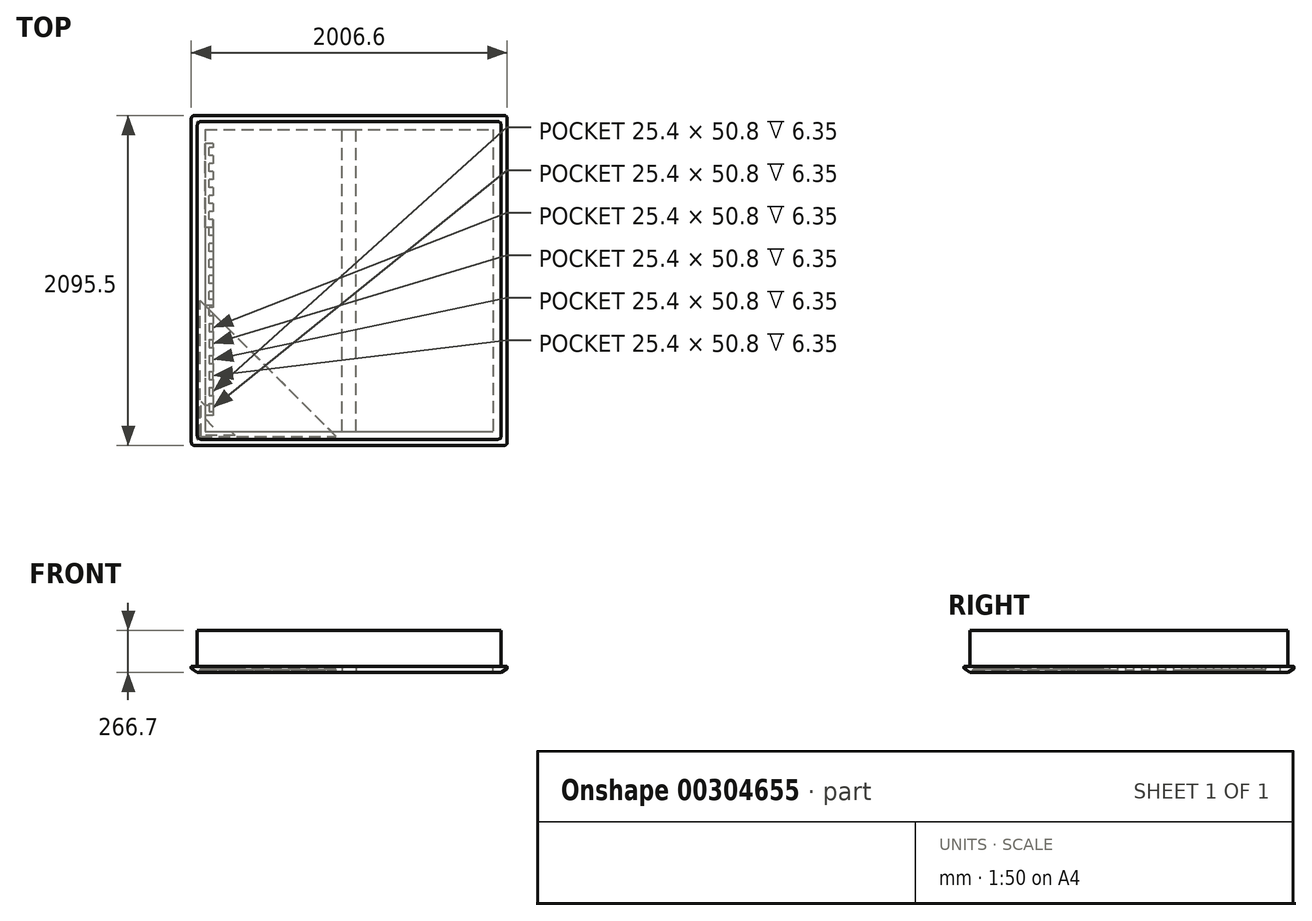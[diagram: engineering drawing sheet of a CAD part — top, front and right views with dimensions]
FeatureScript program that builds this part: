
annotation { "Feature Type Name" : "Feature", "Feature Type Description" : "" }
export const myFeature = defineFeature(function(context is Context, id is Id, definition is map)
    precondition{}
    {
        {
            var Q0;
            Q0=qCreatedBy(makeId("Top.planeOp"),FACE);
            var sketch = newSketch(context, id + "F0", { "sketchPlane" : qUnion([Q0])});
            skLineSegment(sketch, "E0.bottom", {"start": v(-965.2, 1009.65) * mm, "end": v(965.2, 1009.65) * mm});
            skLineSegment(sketch, "E0.top", {"start": v(-965.2, -1009.65) * mm, "end": v(965.2, -1009.65) * mm});
            skLineSegment(sketch, "E0.left", {"start": v(-965.2, 1009.65) * mm, "end": v(-965.2, -1009.65) * mm});
            skLineSegment(sketch, "E0.right", {"start": v(965.2, 1009.65) * mm, "end": v(965.2, -1009.65) * mm});
            skLineSegment(sketch, "E1", {"start": v(-965.2, 1009.65) * mm, "end": v(965.2, -1009.65) * mm, "construction": true});
            skSolve(sketch);
        }
        {
            var Q0;
            Q0=makeQuery(id+"F0.imprint","IMPRINT",FACE,{"disambiguationData":[TD([[makeQuery(id+"F0.imprint","IMPRINT",EDGE,{"derivedFrom":sQuery(id+"F0.wireOp",EDGE,"E0.bottom")}),-1.0]])]});
            extrude(context, id + "F1", {"entities" : qUnion([Q0]), "depth" : 228.6 * mm});
        }
        {
            var Q0;
            Q0=makeQuery(id+"F1.opExtrude","SWEPT_EDGE",EDGE,{"disambiguationData":[OSD([sQuery(id+"F0.wireOp",EDGE,"E0.bottom"),sQuery(id+"F0.wireOp",EDGE,"E0.right")])]});
            var Q1;
            Q1=makeQuery(id+"F1.opExtrude","SWEPT_EDGE",EDGE,{"disambiguationData":[OSD([sQuery(id+"F0.wireOp",EDGE,"E0.top"),sQuery(id+"F0.wireOp",EDGE,"E0.left")])]});
            var Q2;
            Q2=makeQuery(id+"F1.opExtrude","SWEPT_EDGE",EDGE,{"disambiguationData":[OSD([sQuery(id+"F0.wireOp",EDGE,"E0.top"),sQuery(id+"F0.wireOp",EDGE,"E0.right")])]});
            var Q3;
            Q3=makeQuery(id+"F1.opExtrude","SWEPT_EDGE",EDGE,{"disambiguationData":[OSD([sQuery(id+"F0.wireOp",EDGE,"E0.bottom"),sQuery(id+"F0.wireOp",EDGE,"E0.left")])]});
            fillet(context, id + "F2", {"entities" : qUnion([Q0, Q1, Q2, Q3]), "radius" : 25.4 * mm, "tangentPropagation" : true, "allowEdgeOverflow" : false});
        }
        {
            var Q0;
            Q0=qCreatedBy(makeId("Top.planeOp"),FACE);
            var sketch = newSketch(context, id + "F3", { "sketchPlane" : qUnion([Q0])});
            skLineSegment(sketch, "E2.bottom", {"start": v(-1003.3, 1047.75) * mm, "end": v(1003.3, 1047.75) * mm});
            skLineSegment(sketch, "E2.top", {"start": v(-1003.3, -1047.75) * mm, "end": v(1003.3, -1047.75) * mm});
            skLineSegment(sketch, "E2.left", {"start": v(-1003.3, 1047.75) * mm, "end": v(-1003.3, -1047.75) * mm});
            skLineSegment(sketch, "E2.right", {"start": v(1003.3, 1047.75) * mm, "end": v(1003.3, -1047.75) * mm});
            skLineSegment(sketch, "E3.0", {"start": v(-914.4, 958.85) * mm, "end": v(914.4, 958.85) * mm});
            skLineSegment(sketch, "E3.1", {"start": v(-914.4, 958.85) * mm, "end": v(-914.4, -958.85) * mm});
            skLineSegment(sketch, "E3.2", {"start": v(-914.4, -958.85) * mm, "end": v(914.4, -958.85) * mm});
            skLineSegment(sketch, "E3.3", {"start": v(914.4, 958.85) * mm, "end": v(914.4, -958.85) * mm});
            skSolve(sketch);
        }
        {
            var Q0;
            Q0 = qSketchRegion(id + "F3", true);
            extrude(context, id + "F4", {"entities" : qUnion([Q0]), "oppositeDirection" : true, "depth" : 38.1 * mm});
        }
        {
            var Q0;
            Q0=makeQuery(id+"F4.opExtrude","CAP_EDGE",EDGE,{"disambiguationData":[OSD([sQuery(id+"F3.wireOp",EDGE,"E2.left")])],"isStart":false});
            var Q1;
            Q1=makeQuery(id+"F4.opExtrude","CAP_EDGE",EDGE,{"disambiguationData":[OSD([sQuery(id+"F3.wireOp",EDGE,"E2.bottom")])],"isStart":false});
            var Q2;
            Q2=makeQuery(id+"F4.opExtrude","CAP_EDGE",EDGE,{"disambiguationData":[OSD([sQuery(id+"F3.wireOp",EDGE,"E2.top")])],"isStart":false});
            var Q3;
            Q3=makeQuery(id+"F4.opExtrude","CAP_EDGE",EDGE,{"disambiguationData":[OSD([sQuery(id+"F3.wireOp",EDGE,"E2.right")])],"isStart":false});
            chamfer(context, id + "F5", {"entities" : qUnion([Q0, Q1, Q2, Q3]), "chamferType" : ChamferType.TWO_OFFSETS, "width1" : 25.4 * mm, "oppositeDirection" : false, "width2" : 38.1 * mm, "tangentPropagation" : true});
        }
        {
            var Q0;
            Q0=makeQuery(id+"F4.opExtrude","SWEPT_EDGE",EDGE,{"disambiguationData":[OSD([sQuery(id+"F3.wireOp",EDGE,"E2.top"),sQuery(id+"F3.wireOp",EDGE,"E2.right")])]});
            var Q1;
            Q1=makeQuery(id+"F4.opExtrude","SWEPT_EDGE",EDGE,{"disambiguationData":[OSD([sQuery(id+"F3.wireOp",EDGE,"E2.bottom"),sQuery(id+"F3.wireOp",EDGE,"E2.right")])]});
            var Q2;
            Q2=makeQuery(id+"F4.opExtrude","SWEPT_EDGE",EDGE,{"disambiguationData":[OSD([sQuery(id+"F3.wireOp",EDGE,"E2.bottom"),sQuery(id+"F3.wireOp",EDGE,"E2.left")])]});
            var Q3;
            Q3=makeQuery(id+"F4.opExtrude","SWEPT_EDGE",EDGE,{"disambiguationData":[OSD([sQuery(id+"F3.wireOp",EDGE,"E2.top"),sQuery(id+"F3.wireOp",EDGE,"E2.left")])]});
            fillet(context, id + "F6", {"entities" : qUnion([Q0, Q1, Q2, Q3]), "radius" : 19.05 * mm, "allowEdgeOverflow" : false});
        }
        {
            var Q0;
            {var subQ0=sQuery(id+"F3.wireOp",EDGE,"E2.bottom");Q0=makeQuery(id+"F5.opChamfer","BLEND_EDGE",EDGE,{"blendedFrom":[makeQuery(id+"F4.opExtrude","CAP_EDGE",EDGE,{"disambiguationData":[OSD([subQ0])],"isStart":false}),makeQuery(id+"F4.opExtrude","SWEPT_FACE",FACE,{"disambiguationData":[OSD([subQ0])]})],"blendedInto":[makeQuery(id+"F4.opExtrude","SWEPT_FACE",FACE,{"disambiguationData":[OSD([subQ0])]})]});}
            var Q1;
            Q1=makeQuery(id+"F4.opExtrude","CAP_EDGE",EDGE,{"disambiguationData":[OSD([sQuery(id+"F3.wireOp",EDGE,"E2.bottom")])],"isStart":true});
            var Q2;
            Q2=makeQuery(id+"F4.opExtrude","CAP_EDGE",EDGE,{"disambiguationData":[OSD([sQuery(id+"F3.wireOp",EDGE,"E2.left")])],"isStart":true});
            var Q3;
            {var subQ0=sQuery(id+"F3.wireOp",EDGE,"E2.left");Q3=makeQuery(id+"F5.opChamfer","BLEND_EDGE",EDGE,{"blendedFrom":[makeQuery(id+"F4.opExtrude","CAP_EDGE",EDGE,{"disambiguationData":[OSD([subQ0])],"isStart":false}),makeQuery(id+"F4.opExtrude","SWEPT_FACE",FACE,{"disambiguationData":[OSD([subQ0])]})],"blendedInto":[makeQuery(id+"F4.opExtrude","SWEPT_FACE",FACE,{"disambiguationData":[OSD([subQ0])]})]});}
            var Q4;
            Q4=makeQuery(id+"F4.opExtrude","CAP_EDGE",EDGE,{"disambiguationData":[OSD([sQuery(id+"F3.wireOp",EDGE,"E2.top")])],"isStart":true});
            var Q5;
            {var subQ0=sQuery(id+"F3.wireOp",EDGE,"E2.top");Q5=makeQuery(id+"F5.opChamfer","BLEND_EDGE",EDGE,{"blendedFrom":[makeQuery(id+"F4.opExtrude","CAP_EDGE",EDGE,{"disambiguationData":[OSD([subQ0])],"isStart":false}),makeQuery(id+"F4.opExtrude","SWEPT_FACE",FACE,{"disambiguationData":[OSD([subQ0])]})],"blendedInto":[makeQuery(id+"F4.opExtrude","SWEPT_FACE",FACE,{"disambiguationData":[OSD([subQ0])]})]});}
            var Q6;
            {var subQ0=sQuery(id+"F3.wireOp",EDGE,"E2.right");Q6=makeQuery(id+"F5.opChamfer","BLEND_EDGE",EDGE,{"blendedFrom":[makeQuery(id+"F4.opExtrude","CAP_EDGE",EDGE,{"disambiguationData":[OSD([subQ0])],"isStart":false}),makeQuery(id+"F4.opExtrude","SWEPT_FACE",FACE,{"disambiguationData":[OSD([subQ0])]})],"blendedInto":[makeQuery(id+"F4.opExtrude","SWEPT_FACE",FACE,{"disambiguationData":[OSD([subQ0])]})]});}
            var Q7;
            Q7=makeQuery(id+"F4.opExtrude","CAP_EDGE",EDGE,{"disambiguationData":[OSD([sQuery(id+"F3.wireOp",EDGE,"E2.right")])],"isStart":true});
            var Q8;
            Q8=makeQuery(id+"F5.opChamfer","BLEND_EDGE",EDGE,{"blendedFrom":[makeQuery(id+"F4.opExtrude","CAP_EDGE",EDGE,{"disambiguationData":[OSD([sQuery(id+"F3.wireOp",EDGE,"E2.top")])],"isStart":false}),makeQuery(id+"F4.opExtrude","CAP_EDGE",EDGE,{"disambiguationData":[OSD([sQuery(id+"F3.wireOp",EDGE,"E2.right")])],"isStart":false})],"blendedInto":[]});
            var Q9;
            Q9=makeQuery(id+"F4.opExtrude","SWEPT_EDGE",EDGE,{"disambiguationData":[OSD([sQuery(id+"F3.wireOp",EDGE,"E2.top"),sQuery(id+"F3.wireOp",EDGE,"E2.right")])]});
            var Q10;
            Q10=makeQuery(id+"F4.opExtrude","SWEPT_EDGE",EDGE,{"disambiguationData":[OSD([sQuery(id+"F3.wireOp",EDGE,"E2.bottom"),sQuery(id+"F3.wireOp",EDGE,"E2.right")])]});
            var Q11;
            Q11=makeQuery(id+"F5.opChamfer","BLEND_EDGE",EDGE,{"blendedFrom":[makeQuery(id+"F4.opExtrude","CAP_EDGE",EDGE,{"disambiguationData":[OSD([sQuery(id+"F3.wireOp",EDGE,"E2.bottom")])],"isStart":false}),makeQuery(id+"F4.opExtrude","CAP_EDGE",EDGE,{"disambiguationData":[OSD([sQuery(id+"F3.wireOp",EDGE,"E2.right")])],"isStart":false})],"blendedInto":[]});
            var Q12;
            Q12=makeQuery(id+"F4.opExtrude","SWEPT_EDGE",EDGE,{"disambiguationData":[OSD([sQuery(id+"F3.wireOp",EDGE,"E2.bottom"),sQuery(id+"F3.wireOp",EDGE,"E2.left")])]});
            var Q13;
            Q13=makeQuery(id+"F5.opChamfer","BLEND_EDGE",EDGE,{"blendedFrom":[makeQuery(id+"F4.opExtrude","CAP_EDGE",EDGE,{"disambiguationData":[OSD([sQuery(id+"F3.wireOp",EDGE,"E2.bottom")])],"isStart":false}),makeQuery(id+"F4.opExtrude","CAP_EDGE",EDGE,{"disambiguationData":[OSD([sQuery(id+"F3.wireOp",EDGE,"E2.left")])],"isStart":false})],"blendedInto":[]});
            var Q14;
            Q14=makeQuery(id+"F4.opExtrude","SWEPT_EDGE",EDGE,{"disambiguationData":[OSD([sQuery(id+"F3.wireOp",EDGE,"E2.top"),sQuery(id+"F3.wireOp",EDGE,"E2.left")])]});
            var Q15;
            Q15=makeQuery(id+"F5.opChamfer","BLEND_EDGE",EDGE,{"blendedFrom":[makeQuery(id+"F4.opExtrude","CAP_EDGE",EDGE,{"disambiguationData":[OSD([sQuery(id+"F3.wireOp",EDGE,"E2.top")])],"isStart":false}),makeQuery(id+"F4.opExtrude","CAP_EDGE",EDGE,{"disambiguationData":[OSD([sQuery(id+"F3.wireOp",EDGE,"E2.left")])],"isStart":false})],"blendedInto":[]});
            fillet(context, id + "F7", {"entities" : qUnion([Q0, Q1, Q2, Q3, Q4, Q5, Q6, Q7, Q8, Q9, Q10, Q11, Q12, Q13, Q14, Q15]), "radius" : 2.22 * mm, "tangentPropagation" : true, "allowEdgeOverflow" : false});
        }
        {
            var Q0;
            Q0=makeQuery(id+"F4.opExtrude","CAP_FACE",FACE,{"disambiguationData":[OSD([sQuery(id+"F3.wireOp",EDGE,"E2.bottom"),sQuery(id+"F3.wireOp",EDGE,"E2.top"),sQuery(id+"F3.wireOp",EDGE,"E2.left"),sQuery(id+"F3.wireOp",EDGE,"E2.right"),sQuery(id+"F3.wireOp",EDGE,"E3.0"),sQuery(id+"F3.wireOp",EDGE,"E3.1"),sQuery(id+"F3.wireOp",EDGE,"E3.2"),sQuery(id+"F3.wireOp",EDGE,"E3.3")])],"isStart":false});
            var sketch = newSketch(context, id + "F8", { "sketchPlane" : qUnion([Q0])});
            skLineSegment(sketch, "E4.bottom", {"start": v(-946.15, 990.6) * mm, "end": v(-84.05, 990.6) * mm});
            skLineSegment(sketch, "E4.left", {"start": v(-946.15, 990.6) * mm, "end": v(-946.15, 128.5) * mm});
            skLineSegment(sketch, "E5", {"start": v(-84.05, 990.6) * mm, "end": v(-946.15, 128.5) * mm});
            skSolve(sketch);
        }
        {
            var Q0;
            Q0 = qSketchRegion(id + "F8", true);
            extrude(context, id + "F9", {"entities" : qUnion([Q0]), "operationType" : NewBodyOperationType.REMOVE, "oppositeDirection" : true, "depth" : 19.05 * mm});
        }
        {
            var Q0;
            Q0=makeQuery(id+"F9.boolean.opBoolean","COPY",FACE,{"derivedFrom":makeQuery(id+"F9.opExtrude","CAP_FACE",FACE,{"disambiguationData":[OSD([sQuery(id+"F8.wireOp",EDGE,"E4.bottom"),sQuery(id+"F8.wireOp",EDGE,"E4.left"),sQuery(id+"F8.wireOp",EDGE,"E5")])],"isStart":false})});
            var sketch = newSketch(context, id + "F10", { "sketchPlane" : qUnion([Q0])});
            skLineSegment(sketch, "E6.0", {"start": v(-946.15, 990.6) * mm, "end": v(-84.05, 990.6) * mm});
            skLineSegment(sketch, "E6.1", {"start": v(-946.15, 990.6) * mm, "end": v(-946.15, 128.5) * mm});
            skLineSegment(sketch, "E7", {"start": v(-946.15, 128.5) * mm, "end": v(-84.05, 990.6) * mm});
            skSolve(sketch);
        }
        {
            var Q0;
            Q0 = qSketchRegion(id + "F10", true);
            var Q1;
            Q1=makeQuery(id+"F4.opExtrude","CAP_FACE",FACE,{"disambiguationData":[OSD([sQuery(id+"F3.wireOp",EDGE,"E2.bottom"),sQuery(id+"F3.wireOp",EDGE,"E2.top"),sQuery(id+"F3.wireOp",EDGE,"E2.left"),sQuery(id+"F3.wireOp",EDGE,"E2.right"),sQuery(id+"F3.wireOp",EDGE,"E3.0"),sQuery(id+"F3.wireOp",EDGE,"E3.1"),sQuery(id+"F3.wireOp",EDGE,"E3.2"),sQuery(id+"F3.wireOp",EDGE,"E3.3")])],"isStart":false});
            extrude(context, id + "F11", {"entities" : qUnion([Q0]), "endBound" : BoundingType.UP_TO_SURFACE, "endBoundEntityFace" : qUnion([Q1]), "depth" : 12.7 * mm});
        }
        {
            var Q0;
            Q0=makeQuery(id+"F4.opExtrude","CAP_FACE",FACE,{"disambiguationData":[OSD([sQuery(id+"F3.wireOp",EDGE,"E2.bottom"),sQuery(id+"F3.wireOp",EDGE,"E2.top"),sQuery(id+"F3.wireOp",EDGE,"E2.left"),sQuery(id+"F3.wireOp",EDGE,"E2.right"),sQuery(id+"F3.wireOp",EDGE,"E3.0"),sQuery(id+"F3.wireOp",EDGE,"E3.1"),sQuery(id+"F3.wireOp",EDGE,"E3.2"),sQuery(id+"F3.wireOp",EDGE,"E3.3")])],"isStart":true});
            var sketch = newSketch(context, id + "F12", { "sketchPlane" : qUnion([Q0])});
            skLineSegment(sketch, "E8", {"start": v(-724.27, -984.25) * mm, "end": v(-939.8, -984.25) * mm});
            skLineSegment(sketch, "E9", {"start": v(-939.8, -984.25) * mm, "end": v(-939.8, -768.72) * mm});
            skLineSegment(sketch, "E10", {"start": v(-939.8, -768.72) * mm, "end": v(-724.27, -984.25) * mm});
            skSolve(sketch);
        }
        {
            var Q0;
            {var subQ1=sQuery(id+"F12.wireOp",EDGE,"E8");Q0=makeQuery(id+"F12.imprint","IMPRINT",FACE,{"disambiguationData":[TD([[makeQuery(id+"F12.imprint","IMPRINT",EDGE,{"derivedFrom":subQ1}),-1.0]])]});}
            extrude(context, id + "F13", {"entities" : qUnion([Q0]), "operationType" : NewBodyOperationType.REMOVE, "oppositeDirection" : true, "depth" : 12.7 * mm});
        }
        {
            var Q0;
            Q0=makeQuery(id+"F13.boolean.opBoolean","COPY",FACE,{"derivedFrom":makeQuery(id+"F13.opExtrude","CAP_FACE",FACE,{"disambiguationData":[OSD([sQuery(id+"F3.wireOp",EDGE,"E3.1"),sQuery(id+"F3.wireOp",EDGE,"E3.2"),sQuery(id+"F12.wireOp",EDGE,"E8"),sQuery(id+"F12.wireOp",EDGE,"E9"),sQuery(id+"F12.wireOp",EDGE,"E10")])],"isStart":false})});
            var sketch = newSketch(context, id + "F14", { "sketchPlane" : qUnion([Q0])});
            skLineSegment(sketch, "E11.0", {"start": v(-939.8, -984.25) * mm, "end": v(-939.8, -768.72) * mm});
            skLineSegment(sketch, "E12.0", {"start": v(-724.27, -984.25) * mm, "end": v(-939.8, -984.25) * mm});
            skLineSegment(sketch, "E13", {"start": v(-939.8, -768.72) * mm, "end": v(-914.4, -794.12) * mm});
            skLineSegment(sketch, "E14", {"start": v(-914.4, -794.12) * mm, "end": v(-914.4, -882.65) * mm});
            skLineSegment(sketch, "E15", {"start": v(-914.4, -876.49) * mm, "end": v(-838.2, -958.85) * mm});
            skLineSegment(sketch, "E16", {"start": v(-838.2, -958.85) * mm, "end": v(-749.67, -958.85) * mm});
            skLineSegment(sketch, "E17", {"start": v(-724.27, -984.25) * mm, "end": v(-749.67, -958.85) * mm});
            skSolve(sketch);
        }
        {
            var Q0;
            Q0=makeQuery(id+"F14.imprint","IMPRINT",FACE,{"disambiguationData":[TD([[makeQuery(id+"F14.imprint","IMPRINT",EDGE,{"derivedFrom":sQuery(id+"F14.wireOp",EDGE,"E11.0")}),-1.0]])]});
            var Q1;
            {var subQ3=sQuery(id+"F14.wireOp",EDGE,"E15");Q1=makeQuery(id+"F14.imprint","IMPRINT",FACE,{"disambiguationData":[TD([[makeQuery(id+"F14.imprint","IMPRINT",EDGE,{"derivedFrom":subQ3}),-1.0]])]});}
            var Q2;
            Q2=makeQuery(id+"F4.opExtrude","CAP_FACE",FACE,{"disambiguationData":[OSD([sQuery(id+"F3.wireOp",EDGE,"E2.bottom"),sQuery(id+"F3.wireOp",EDGE,"E2.top"),sQuery(id+"F3.wireOp",EDGE,"E2.left"),sQuery(id+"F3.wireOp",EDGE,"E2.right"),sQuery(id+"F3.wireOp",EDGE,"E3.0"),sQuery(id+"F3.wireOp",EDGE,"E3.1"),sQuery(id+"F3.wireOp",EDGE,"E3.2"),sQuery(id+"F3.wireOp",EDGE,"E3.3")])],"isStart":true});
            extrude(context, id + "F15", {"entities" : qUnion([Q0, Q1]), "endBound" : BoundingType.UP_TO_SURFACE, "endBoundEntityFace" : qUnion([Q2]), "depth" : 25.4 * mm});
        }
        {
            var Q0;
            Q0=makeQuery(id+"F4.opExtrude","SWEPT_FACE",FACE,{"disambiguationData":[OSD([sQuery(id+"F3.wireOp",EDGE,"E3.1")])]});
            var sketch = newSketch(context, id + "F16", { "sketchPlane" : qUnion([Q0])});
            skLineSegment(sketch, "E18", {"start": v(-857.25, -19.05) * mm, "end": v(-160.25, -19.05) * mm});
            skLineSegment(sketch, "E19", {"start": v(-160.25, -19.05) * mm, "end": v(-160.25, -38.1) * mm});
            skLineSegment(sketch, "E20", {"start": v(-160.25, -38.1) * mm, "end": v(337.1, -38.1) * mm});
            skLineSegment(sketch, "E21", {"start": v(337.1, -38.1) * mm, "end": v(337.1, -19.05) * mm});
            skLineSegment(sketch, "E22", {"start": v(337.1, -19.05) * mm, "end": v(869.5, -19.05) * mm});
            skLineSegment(sketch, "E23", {"start": v(869.5, -19.05) * mm, "end": v(869.5, 0) * mm});
            skLineSegment(sketch, "E24", {"start": v(869.5, 0) * mm, "end": v(-857.25, 0) * mm});
            skLineSegment(sketch, "E25", {"start": v(-857.25, 0) * mm, "end": v(-857.25, -19.05) * mm});
            skSolve(sketch);
        }
        {
            var Q0;
            {var subQ2=sQuery(id+"F16.wireOp",EDGE,"E18");Q0=makeQuery(id+"F16.imprint","IMPRINT",FACE,{"disambiguationData":[TD([[makeQuery(id+"F16.imprint","IMPRINT",EDGE,{"derivedFrom":subQ2}),-1.0]])]});}
            var Q1;
            {var subQ1=sQuery(id+"F3.wireOp",EDGE,"E3.1");var subQ2=makeQuery(id+"F13.boolean.opBoolean","COPY",EDGE,{"derivedFrom":makeQuery(id+"F13.opExtrude","SWEPT_EDGE",EDGE,{"disambiguationData":[OSD([subQ1,sQuery(id+"F12.wireOp",EDGE,"E10")])]})});Q1=makeQuery(id+"F16.imprint","IMPRINT",FACE,{"disambiguationData":[TD([[makeQuery(id+"F16.imprint","IMPRINT",EDGE,{"derivedFrom":subQ2}),1.0]])]});}
            extrude(context, id + "F17", {"entities" : qUnion([Q0, Q1]), "depth" : 50.8 * mm});
        }
        {
            var Q0;
            Q0=makeQuery(id+"F17.opExtrude","SWEPT_FACE",FACE,{"disambiguationData":[OSD([sQuery(id+"F16.wireOp",EDGE,"E24")])]});
            var sketch = newSketch(context, id + "F18", { "sketchPlane" : qUnion([Q0])});
            skLineSegment(sketch, "E26.bottom", {"start": v(-863.6, -831.85) * mm, "end": v(-889, -831.85) * mm});
            skLineSegment(sketch, "E26.top", {"start": v(-863.6, -781.05) * mm, "end": v(-889, -781.05) * mm});
            skLineSegment(sketch, "E26.left", {"start": v(-863.6, -831.85) * mm, "end": v(-863.6, -781.05) * mm});
            skLineSegment(sketch, "E26.right", {"start": v(-889, -831.85) * mm, "end": v(-889, -781.05) * mm});
            skLineSegment(sketch, "E27.0.1.0", {"start": v(-863.6, -679.45) * mm, "end": v(-889, -679.45) * mm});
            skLineSegment(sketch, "E27.0.1.1", {"start": v(-889, -730.25) * mm, "end": v(-889, -679.45) * mm});
            skLineSegment(sketch, "E27.0.1.2", {"start": v(-863.6, -730.25) * mm, "end": v(-863.6, -679.45) * mm});
            skLineSegment(sketch, "E27.0.1.3", {"start": v(-863.6, -730.25) * mm, "end": v(-889, -730.25) * mm});
            skLineSegment(sketch, "E27.0.2.0", {"start": v(-863.6, -577.85) * mm, "end": v(-889, -577.85) * mm});
            skLineSegment(sketch, "E27.0.2.1", {"start": v(-889, -628.65) * mm, "end": v(-889, -577.85) * mm});
            skLineSegment(sketch, "E27.0.2.2", {"start": v(-863.6, -628.65) * mm, "end": v(-863.6, -577.85) * mm});
            skLineSegment(sketch, "E27.0.2.3", {"start": v(-863.6, -628.65) * mm, "end": v(-889, -628.65) * mm});
            skLineSegment(sketch, "E27.0.3.0", {"start": v(-863.6, -476.25) * mm, "end": v(-889, -476.25) * mm});
            skLineSegment(sketch, "E27.0.3.1", {"start": v(-889, -527.05) * mm, "end": v(-889, -476.25) * mm});
            skLineSegment(sketch, "E27.0.3.2", {"start": v(-863.6, -527.05) * mm, "end": v(-863.6, -476.25) * mm});
            skLineSegment(sketch, "E27.0.3.3", {"start": v(-863.6, -527.05) * mm, "end": v(-889, -527.05) * mm});
            skLineSegment(sketch, "E27.0.4.0", {"start": v(-863.6, -374.65) * mm, "end": v(-889, -374.65) * mm});
            skLineSegment(sketch, "E27.0.4.1", {"start": v(-889, -425.45) * mm, "end": v(-889, -374.65) * mm});
            skLineSegment(sketch, "E27.0.4.2", {"start": v(-863.6, -425.45) * mm, "end": v(-863.6, -374.65) * mm});
            skLineSegment(sketch, "E27.0.4.3", {"start": v(-863.6, -425.45) * mm, "end": v(-889, -425.45) * mm});
            skLineSegment(sketch, "E27.0.5.0", {"start": v(-863.6, -273.05) * mm, "end": v(-889, -273.05) * mm});
            skLineSegment(sketch, "E27.0.5.1", {"start": v(-889, -323.85) * mm, "end": v(-889, -273.05) * mm});
            skLineSegment(sketch, "E27.0.5.2", {"start": v(-863.6, -323.85) * mm, "end": v(-863.6, -273.05) * mm});
            skLineSegment(sketch, "E27.0.5.3", {"start": v(-863.6, -323.85) * mm, "end": v(-889, -323.85) * mm});
            skLineSegment(sketch, "E27.0.6.0", {"start": v(-863.6, -171.45) * mm, "end": v(-889, -171.45) * mm});
            skLineSegment(sketch, "E27.0.6.1", {"start": v(-889, -222.25) * mm, "end": v(-889, -171.45) * mm});
            skLineSegment(sketch, "E27.0.6.2", {"start": v(-863.6, -222.25) * mm, "end": v(-863.6, -171.45) * mm});
            skLineSegment(sketch, "E27.0.6.3", {"start": v(-863.6, -222.25) * mm, "end": v(-889, -222.25) * mm});
            skLineSegment(sketch, "E27.0.7.0", {"start": v(-863.6, -69.85) * mm, "end": v(-889, -69.85) * mm});
            skLineSegment(sketch, "E27.0.7.1", {"start": v(-889, -120.65) * mm, "end": v(-889, -69.85) * mm});
            skLineSegment(sketch, "E27.0.7.2", {"start": v(-863.6, -120.65) * mm, "end": v(-863.6, -69.85) * mm});
            skLineSegment(sketch, "E27.0.7.3", {"start": v(-863.6, -120.65) * mm, "end": v(-889, -120.65) * mm});
            skLineSegment(sketch, "E27.0.8.0", {"start": v(-863.6, 31.75) * mm, "end": v(-889, 31.75) * mm});
            skLineSegment(sketch, "E27.0.8.1", {"start": v(-889, -19.05) * mm, "end": v(-889, 31.75) * mm});
            skLineSegment(sketch, "E27.0.8.2", {"start": v(-863.6, -19.05) * mm, "end": v(-863.6, 31.75) * mm});
            skLineSegment(sketch, "E27.0.8.3", {"start": v(-863.6, -19.05) * mm, "end": v(-889, -19.05) * mm});
            skLineSegment(sketch, "E27.0.9.0", {"start": v(-863.6, 133.35) * mm, "end": v(-889, 133.35) * mm});
            skLineSegment(sketch, "E27.0.9.1", {"start": v(-889, 82.55) * mm, "end": v(-889, 133.35) * mm});
            skLineSegment(sketch, "E27.0.9.2", {"start": v(-863.6, 82.55) * mm, "end": v(-863.6, 133.35) * mm});
            skLineSegment(sketch, "E27.0.9.3", {"start": v(-863.6, 82.55) * mm, "end": v(-889, 82.55) * mm});
            skLineSegment(sketch, "E27.0.10.0", {"start": v(-863.6, 234.95) * mm, "end": v(-889, 234.95) * mm});
            skLineSegment(sketch, "E27.0.10.1", {"start": v(-889, 184.15) * mm, "end": v(-889, 234.95) * mm});
            skLineSegment(sketch, "E27.0.10.2", {"start": v(-863.6, 184.15) * mm, "end": v(-863.6, 234.95) * mm});
            skLineSegment(sketch, "E27.0.10.3", {"start": v(-863.6, 184.15) * mm, "end": v(-889, 184.15) * mm});
            skLineSegment(sketch, "E27.0.11.0", {"start": v(-863.6, 336.55) * mm, "end": v(-889, 336.55) * mm});
            skLineSegment(sketch, "E27.0.11.1", {"start": v(-889, 285.75) * mm, "end": v(-889, 336.55) * mm});
            skLineSegment(sketch, "E27.0.11.2", {"start": v(-863.6, 285.75) * mm, "end": v(-863.6, 336.55) * mm});
            skLineSegment(sketch, "E27.0.11.3", {"start": v(-863.6, 285.75) * mm, "end": v(-889, 285.75) * mm});
            skLineSegment(sketch, "E27.0.12.0", {"start": v(-863.6, 438.15) * mm, "end": v(-889, 438.15) * mm});
            skLineSegment(sketch, "E27.0.12.1", {"start": v(-889, 387.35) * mm, "end": v(-889, 438.15) * mm});
            skLineSegment(sketch, "E27.0.12.2", {"start": v(-863.6, 387.35) * mm, "end": v(-863.6, 438.15) * mm});
            skLineSegment(sketch, "E27.0.12.3", {"start": v(-863.6, 387.35) * mm, "end": v(-889, 387.35) * mm});
            skLineSegment(sketch, "E27.0.13.0", {"start": v(-863.6, 539.75) * mm, "end": v(-889, 539.75) * mm});
            skLineSegment(sketch, "E27.0.13.1", {"start": v(-889, 488.95) * mm, "end": v(-889, 539.75) * mm});
            skLineSegment(sketch, "E27.0.13.2", {"start": v(-863.6, 488.95) * mm, "end": v(-863.6, 539.75) * mm});
            skLineSegment(sketch, "E27.0.13.3", {"start": v(-863.6, 488.95) * mm, "end": v(-889, 488.95) * mm});
            skLineSegment(sketch, "E27.0.14.0", {"start": v(-863.6, 641.35) * mm, "end": v(-889, 641.35) * mm});
            skLineSegment(sketch, "E27.0.14.1", {"start": v(-889, 590.55) * mm, "end": v(-889, 641.35) * mm});
            skLineSegment(sketch, "E27.0.14.2", {"start": v(-863.6, 590.55) * mm, "end": v(-863.6, 641.35) * mm});
            skLineSegment(sketch, "E27.0.14.3", {"start": v(-863.6, 590.55) * mm, "end": v(-889, 590.55) * mm});
            skLineSegment(sketch, "E27.0.15.0", {"start": v(-863.6, 742.95) * mm, "end": v(-889, 742.95) * mm});
            skLineSegment(sketch, "E27.0.15.1", {"start": v(-889, 692.15) * mm, "end": v(-889, 742.95) * mm});
            skLineSegment(sketch, "E27.0.15.2", {"start": v(-863.6, 692.15) * mm, "end": v(-863.6, 742.95) * mm});
            skLineSegment(sketch, "E27.0.15.3", {"start": v(-863.6, 692.15) * mm, "end": v(-889, 692.15) * mm});
            skLineSegment(sketch, "E27.0.16.0", {"start": v(-863.6, 844.55) * mm, "end": v(-889, 844.55) * mm});
            skLineSegment(sketch, "E27.0.16.1", {"start": v(-889, 793.75) * mm, "end": v(-889, 844.55) * mm});
            skLineSegment(sketch, "E27.0.16.2", {"start": v(-863.6, 793.75) * mm, "end": v(-863.6, 844.55) * mm});
            skLineSegment(sketch, "E27.0.16.3", {"start": v(-863.6, 793.75) * mm, "end": v(-889, 793.75) * mm});
            skLineSegment(sketch, "E27.direction1", {"start": v(-889, -831.85) * mm, "end": v(-863.6, -831.85) * mm, "construction": true});
            skLineSegment(sketch, "E27.direction2", {"start": v(-889, -831.85) * mm, "end": v(-889, -730.25) * mm, "construction": true});
            skSolve(sketch);
        }
        {
            var Q0;
            Q0 = qSketchRegion(id + "F18", true);
            extrude(context, id + "F19", {"entities" : qUnion([Q0]), "operationType" : NewBodyOperationType.REMOVE, "oppositeDirection" : true, "depth" : 25.4 * mm});
        }
        {
            var Q0;
            Q0=makeQuery(id+"F4.opExtrude","SWEPT_FACE",FACE,{"disambiguationData":[OSD([sQuery(id+"F3.wireOp",EDGE,"E3.0")])]});
            var sketch = newSketch(context, id + "F20", { "sketchPlane" : qUnion([Q0])});
            skLineSegment(sketch, "E28.bottom", {"start": v(-44.45, 0) * mm, "end": v(44.45, 0) * mm});
            skLineSegment(sketch, "E28.top", {"start": v(-44.45, -38.1) * mm, "end": v(44.45, -38.1) * mm});
            skLineSegment(sketch, "E28.left", {"start": v(-44.45, 0) * mm, "end": v(-44.45, -38.1) * mm});
            skLineSegment(sketch, "E28.right", {"start": v(44.45, 0) * mm, "end": v(44.45, -38.1) * mm});
            skSolve(sketch);
        }
        {
            var Q0;
            Q0=makeQuery(id+"F20.imprint","IMPRINT",FACE,{"disambiguationData":[TD([[makeQuery(id+"F20.imprint","IMPRINT",EDGE,{"derivedFrom":sQuery(id+"F20.wireOp",EDGE,"E28.bottom")}),-1.0]])]});
            extrude(context, id + "F21", {"entities" : qUnion([Q0]), "endBound" : BoundingType.UP_TO_NEXT, "depth" : 25.4 * mm});
        }
    });
